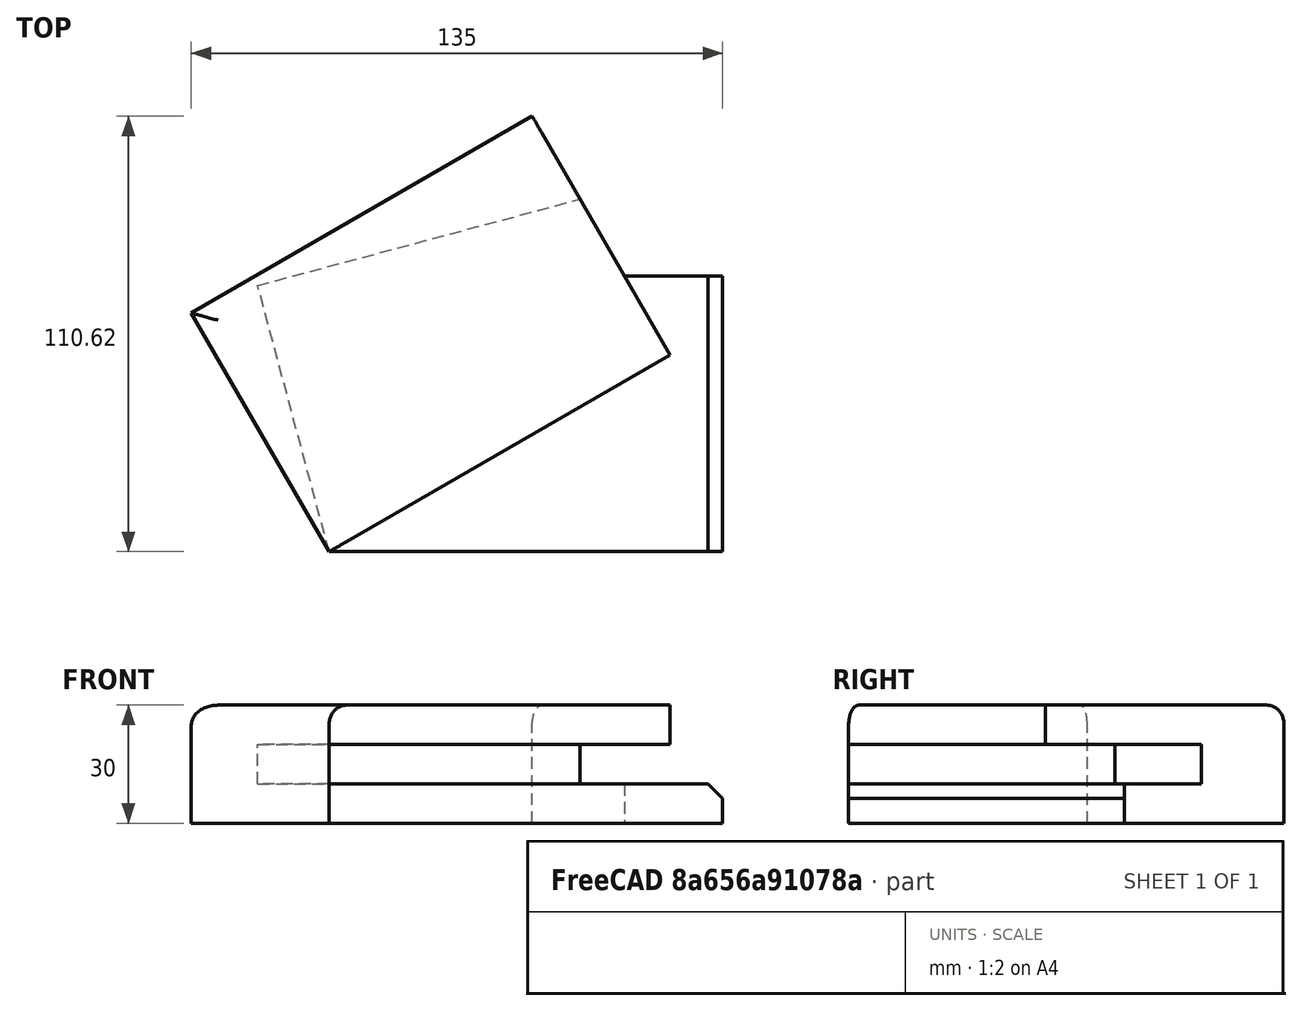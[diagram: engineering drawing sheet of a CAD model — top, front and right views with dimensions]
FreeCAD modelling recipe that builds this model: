
FCSTD DOCUMENT  (FreeCAD 0.17R13523 (Git))
Label: profiling
License: All rights reserved
LicenseURL: http://en.wikipedia.org/wiki/All_rights_reserved
objects: Part::Box×3, Part::MultiFuse×1, Part::Cut×1, PartDesign::Body×1, Part::Chamfer×1, Part::Fillet×1, Part::Feature×1
note: 9 computed .brp shape members not serialized (recipe doc carries the construction recipe); baked Part::Feature solids carry a one-line shape summary decoded from their .brp

FEATURE [Part::Box] Box  label="Cube"
  AttacherType = Attacher::AttachEngine3D
  Height = 10
  Length = 100
  Width = 70
FEATURE [Part::Box] Box001  label="Cube001"
  AttacherType = Attacher::AttachEngine3D
  Height = 10
  Length = 100
  Placement = pos=(0,0,10) rot=(0,0,1;0.261799rad)
  Width = 70
FEATURE [Part::Box] Box002  label="Cube002"
  AttacherType = Attacher::AttachEngine3D
  Height = 30
  Length = 100
  Placement = pos=(0,0,0) rot=(0,0,1;0.523599rad)
  Width = 70
FEATURE [Part::MultiFuse] Fusion
  Shapes = -> [Box,Box002]
FEATURE [Part::Cut] Cut
  Base = -> Fusion
  Tool = -> Box001
FEATURE [PartDesign::Body] Body
  Origin = -> BodyOrigin
FEATURE [Part::Chamfer] Chamfer
  Base = -> Cut
  Edges = 1 edges r=3.7: [Edge2]
FEATURE [Part::Fillet] Fillet
  Base = -> Chamfer
  Edges = 2 edges r=5: [Edge28,Edge45]
FEATURE [Part::Feature] Fillet001
  shape: bbox 135 x 110.6 x 30 mm, 18 faces (baked)
